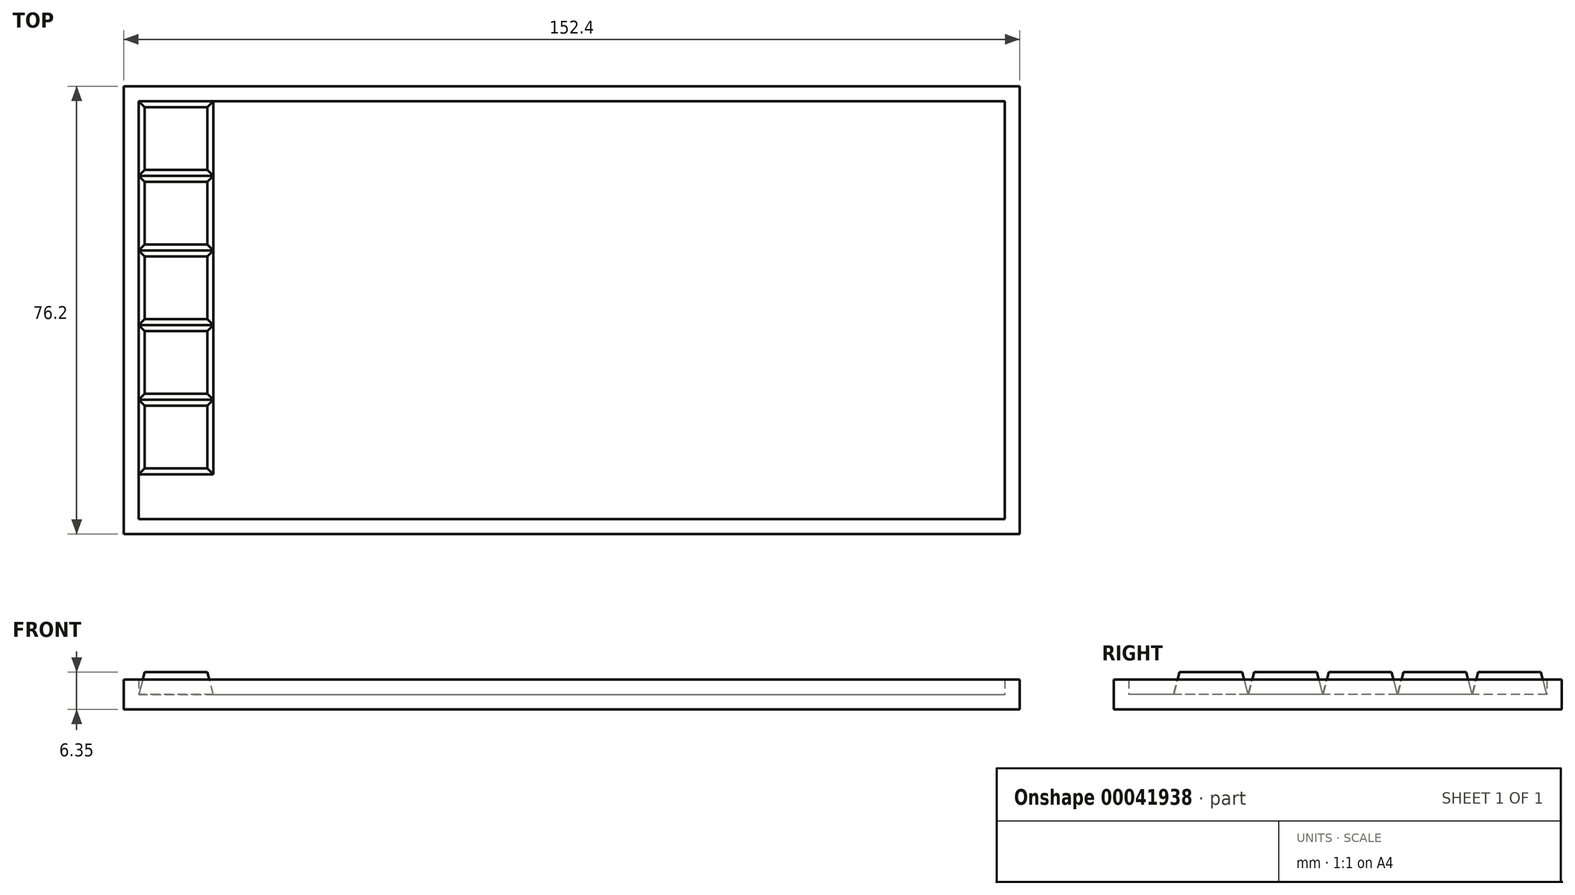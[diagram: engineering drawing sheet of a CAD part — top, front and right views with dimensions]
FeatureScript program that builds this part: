
annotation { "Feature Type Name" : "Feature", "Feature Type Description" : "" }
export const myFeature = defineFeature(function(context is Context, id is Id, definition is map)
    precondition{}
    {
        {
            var Q0;
            Q0=qCreatedBy(makeId("Top.planeOp"),FACE);
            var sketch = newSketch(context, id + "F0", { "sketchPlane" : qUnion([Q0])});
            skLineSegment(sketch, "E0.bottom", {"start": v(-116.38, 20.8) * mm, "end": v(36.02, 20.8) * mm});
            skLineSegment(sketch, "E0.top", {"start": v(-116.38, -55.4) * mm, "end": v(36.02, -55.4) * mm});
            skLineSegment(sketch, "E0.left", {"start": v(-116.38, 20.8) * mm, "end": v(-116.38, -55.4) * mm});
            skLineSegment(sketch, "E0.right", {"start": v(36.02, 20.8) * mm, "end": v(36.02, -55.4) * mm});
            skSolve(sketch);
        }
        {
            var Q0;
            Q0 = qSketchRegion(id + "F0", true);
            var Q1;
            Q1=makeQuery(id+"F0.imprint","IMPRINT",FACE,{"disambiguationData":[TD([[makeQuery(id+"F0.imprint","IMPRINT",EDGE,{"derivedFrom":sQuery(id+"F0.wireOp",EDGE,"E0.bottom")}),-1.0]])]});
            extrude(context, id + "F1", {"entities" : qUnion([Q0, Q1]), "depth" : 5.08 * mm});
        }
        {
            var Q0;
            Q0=makeQuery(id+"F1.opExtrude","CAP_FACE",FACE,{"disambiguationData":[OSD([sQuery(id+"F0.wireOp",EDGE,"E0.bottom"),sQuery(id+"F0.wireOp",EDGE,"E0.top"),sQuery(id+"F0.wireOp",EDGE,"E0.left"),sQuery(id+"F0.wireOp",EDGE,"E0.right")])],"isStart":false});
            shell(context, id + "F2", {"entities" : qUnion([Q0]), "thickness" : 2.54 * mm});
        }
        {
            var Q0;
            Q0=makeQuery(id+"F2.opShell","OFFSET_FACE",FACE,{"disambiguationData":[OSD([sQuery(id+"F0.wireOp",EDGE,"E0.bottom"),sQuery(id+"F0.wireOp",EDGE,"E0.top"),sQuery(id+"F0.wireOp",EDGE,"E0.left"),sQuery(id+"F0.wireOp",EDGE,"E0.right")])]});
            var sketch = newSketch(context, id + "F3", { "sketchPlane" : qUnion([Q0])});
            skLineSegment(sketch, "E1.bottom", {"start": v(-113.84, 18.27) * mm, "end": v(-101.14, 18.27) * mm});
            skLineSegment(sketch, "E1.top", {"start": v(-113.84, 5.57) * mm, "end": v(-101.14, 5.57) * mm});
            skLineSegment(sketch, "E1.left", {"start": v(-113.84, 18.27) * mm, "end": v(-113.84, 5.57) * mm});
            skLineSegment(sketch, "E1.right", {"start": v(-101.14, 18.27) * mm, "end": v(-101.14, 5.57) * mm});
            skSolve(sketch);
        }
        {
            var Q0;
            Q0=makeQuery(id+"F3.imprint","IMPRINT",FACE,{"disambiguationData":[TD([[makeQuery(id+"F3.imprint","IMPRINT",EDGE,{"derivedFrom":sQuery(id+"F3.wireOp",EDGE,"E1.bottom")}),-1.0]])]});
            extrude(context, id + "F4", {"entities" : qUnion([Q0]), "operationType" : NewBodyOperationType.ADD, "depth" : 3.8 * mm, "hasDraft" : true, "draftAngle" : 15 * degree, "draftPullDirection" : true});
        }
        {
            var Q0;
            Q0=makeQuery(id+"F2.opShell","OFFSET_FACE",FACE,{"disambiguationData":[OSD([sQuery(id+"F0.wireOp",EDGE,"E0.bottom"),sQuery(id+"F0.wireOp",EDGE,"E0.top"),sQuery(id+"F0.wireOp",EDGE,"E0.left"),sQuery(id+"F0.wireOp",EDGE,"E0.right")])]});
            var sketch = newSketch(context, id + "F5", { "sketchPlane" : qUnion([Q0])});
            skLineSegment(sketch, "E2.bottom", {"start": v(-113.84, 5.57) * mm, "end": v(-101.14, 5.57) * mm});
            skLineSegment(sketch, "E2.top", {"start": v(-113.84, -7.13) * mm, "end": v(-101.14, -7.13) * mm});
            skLineSegment(sketch, "E2.left", {"start": v(-113.84, 5.57) * mm, "end": v(-113.84, -7.13) * mm});
            skLineSegment(sketch, "E2.right", {"start": v(-101.14, 5.57) * mm, "end": v(-101.14, -7.13) * mm});
            skSolve(sketch);
        }
        {
            var Q0;
            Q0 = qSketchRegion(id + "F5", true);
            var Q1;
            Q1=makeQuery(id+"F5.imprint","IMPRINT",FACE,{"disambiguationData":[TD([[makeQuery(id+"F5.imprint","IMPRINT",EDGE,{"derivedFrom":sQuery(id+"F5.wireOp",EDGE,"E2.bottom")}),-1.0]])]});
            extrude(context, id + "F6", {"entities" : qUnion([Q0, Q1]), "operationType" : NewBodyOperationType.ADD, "depth" : 3.8 * mm, "hasDraft" : true, "draftAngle" : 15 * degree, "draftPullDirection" : true});
        }
        {
            var Q0;
            Q0=makeQuery(id+"F2.opShell","OFFSET_FACE",FACE,{"disambiguationData":[OSD([sQuery(id+"F0.wireOp",EDGE,"E0.bottom"),sQuery(id+"F0.wireOp",EDGE,"E0.top"),sQuery(id+"F0.wireOp",EDGE,"E0.left"),sQuery(id+"F0.wireOp",EDGE,"E0.right")])]});
            var sketch = newSketch(context, id + "F7", { "sketchPlane" : qUnion([Q0])});
            skLineSegment(sketch, "E3.bottom", {"start": v(-113.84, -7.13) * mm, "end": v(-101.14, -7.13) * mm});
            skLineSegment(sketch, "E3.top", {"start": v(-113.84, -19.83) * mm, "end": v(-101.14, -19.83) * mm});
            skLineSegment(sketch, "E3.left", {"start": v(-113.84, -7.13) * mm, "end": v(-113.84, -19.83) * mm});
            skLineSegment(sketch, "E3.right", {"start": v(-101.14, -7.13) * mm, "end": v(-101.14, -19.83) * mm});
            skSolve(sketch);
        }
        {
            var Q0;
            Q0=makeQuery(id+"F7.imprint","IMPRINT",FACE,{"disambiguationData":[TD([[makeQuery(id+"F7.imprint","IMPRINT",EDGE,{"derivedFrom":sQuery(id+"F7.wireOp",EDGE,"E3.bottom")}),-1.0]])]});
            extrude(context, id + "F8", {"entities" : qUnion([Q0]), "operationType" : NewBodyOperationType.ADD, "depth" : 3.8 * mm, "hasDraft" : true, "draftAngle" : 15 * degree, "draftPullDirection" : true});
        }
        {
            var Q0;
            Q0=makeQuery(id+"F2.opShell","OFFSET_FACE",FACE,{"disambiguationData":[OSD([sQuery(id+"F0.wireOp",EDGE,"E0.bottom"),sQuery(id+"F0.wireOp",EDGE,"E0.top"),sQuery(id+"F0.wireOp",EDGE,"E0.left"),sQuery(id+"F0.wireOp",EDGE,"E0.right")])]});
            var sketch = newSketch(context, id + "F9", { "sketchPlane" : qUnion([Q0])});
            skLineSegment(sketch, "E4.bottom", {"start": v(-113.84, -19.83) * mm, "end": v(-101.14, -19.83) * mm});
            skLineSegment(sketch, "E4.top", {"start": v(-113.84, -32.53) * mm, "end": v(-101.14, -32.53) * mm});
            skLineSegment(sketch, "E4.left", {"start": v(-113.84, -19.83) * mm, "end": v(-113.84, -32.53) * mm});
            skLineSegment(sketch, "E4.right", {"start": v(-101.14, -19.83) * mm, "end": v(-101.14, -32.53) * mm});
            skSolve(sketch);
        }
        {
            var Q0;
            Q0=makeQuery(id+"F9.imprint","IMPRINT",FACE,{"disambiguationData":[TD([[makeQuery(id+"F9.imprint","IMPRINT",EDGE,{"derivedFrom":sQuery(id+"F9.wireOp",EDGE,"E4.bottom")}),-1.0]])]});
            extrude(context, id + "F10", {"entities" : qUnion([Q0]), "operationType" : NewBodyOperationType.ADD, "depth" : 3.8 * mm, "hasDraft" : true, "draftAngle" : 15 * degree, "draftPullDirection" : true});
        }
        {
            var Q0;
            Q0=makeQuery(id+"F2.opShell","OFFSET_FACE",FACE,{"disambiguationData":[OSD([sQuery(id+"F0.wireOp",EDGE,"E0.bottom"),sQuery(id+"F0.wireOp",EDGE,"E0.top"),sQuery(id+"F0.wireOp",EDGE,"E0.left"),sQuery(id+"F0.wireOp",EDGE,"E0.right")])]});
            var sketch = newSketch(context, id + "F11", { "sketchPlane" : qUnion([Q0])});
            skLineSegment(sketch, "E5.bottom", {"start": v(-113.84, -32.53) * mm, "end": v(-101.14, -32.53) * mm});
            skLineSegment(sketch, "E5.top", {"start": v(-113.84, -45.23) * mm, "end": v(-101.14, -45.23) * mm});
            skLineSegment(sketch, "E5.left", {"start": v(-113.84, -32.53) * mm, "end": v(-113.84, -45.23) * mm});
            skLineSegment(sketch, "E5.right", {"start": v(-101.14, -32.53) * mm, "end": v(-101.14, -45.23) * mm});
            skSolve(sketch);
        }
        {
            var Q0;
            {var subQ2=sQuery(id+"F11.wireOp",EDGE,"E5.top");Q0=makeQuery(id+"F11.imprint","IMPRINT",FACE,{"disambiguationData":[TD([[makeQuery(id+"F11.imprint","IMPRINT",EDGE,{"derivedFrom":subQ2}),-1.0]])]});}
            var sketch = newSketch(context, id + "F12", { "sketchPlane" : qUnion([Q0])});
            skSolve(sketch);
        }
        {
            var Q0;
            Q0 = qSketchRegion(id + "F12", true);
            var Q1;
            Q1=makeQuery(id+"F11.imprint","IMPRINT",FACE,{"disambiguationData":[TD([[makeQuery(id+"F11.imprint","IMPRINT",EDGE,{"derivedFrom":sQuery(id+"F11.wireOp",EDGE,"E5.bottom")}),-1.0]])]});
            extrude(context, id + "F13", {"entities" : qUnion([Q0, Q1]), "operationType" : NewBodyOperationType.ADD, "depth" : 3.8 * mm, "hasDraft" : true, "draftAngle" : 15 * degree, "draftPullDirection" : true});
        }
    });
